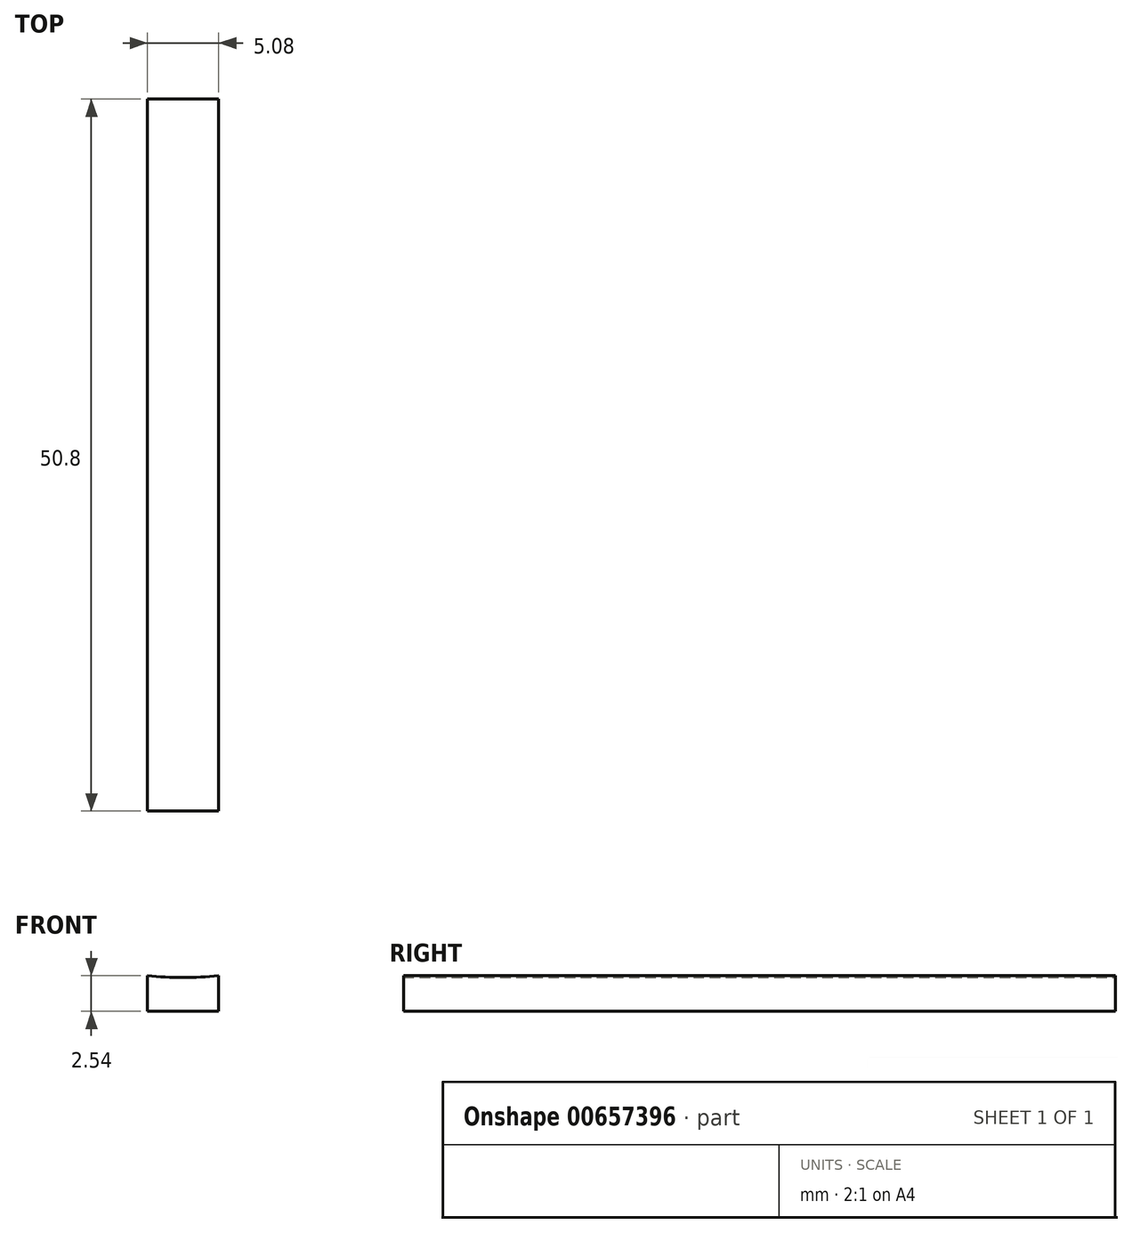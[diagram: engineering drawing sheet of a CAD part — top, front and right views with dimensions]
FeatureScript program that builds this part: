
annotation { "Feature Type Name" : "Feature", "Feature Type Description" : "" }
export const myFeature = defineFeature(function(context is Context, id is Id, definition is map)
    precondition{}
    {
        {
            var Q0;
            Q0=qCreatedBy(makeId("Front.planeOp"),FACE);
            var sketch = newSketch(context, id + "F0", { "sketchPlane" : qUnion([Q0])});
            skCircle(sketch, "E0", {"center": v(0, 25.9) * mm, "radius": 25.4 * mm});
            skLineSegment(sketch, "E1", {"start": v(0, -1.9) * mm, "end": v(-2.54, -1.9) * mm});
            skLineSegment(sketch, "E2", {"start": v(-2.54, -1.9) * mm, "end": v(2.54, -1.9) * mm});
            skLineSegment(sketch, "E3", {"start": v(2.54, -1.9) * mm, "end": v(2.54, 0.63) * mm});
            skLineSegment(sketch, "E4", {"start": v(-2.54, -1.9) * mm, "end": v(-2.54, 0.63) * mm});
            skSolve(sketch);
        }
        {
            var Q0;
            {var subQ0=sQuery(id+"F0.wireOp",EDGE,"E3");Q0=makeQuery(id+"F0.imprint","IMPRINT",FACE,{"disambiguationData":[TD([[makeQuery(id+"F0.imprint","IMPRINT",EDGE,{"derivedFrom":subQ0}),1.0]])]});}
            extrude(context, id + "F1", {"entities" : qUnion([Q0]), "depth" : 50.8 * mm, "offsetDistance" : 25.4 * mm});
        }
    });
